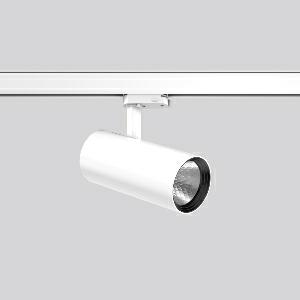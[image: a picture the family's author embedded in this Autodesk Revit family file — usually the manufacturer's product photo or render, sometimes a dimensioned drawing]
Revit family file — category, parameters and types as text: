
# Revit family: deecos_s_mini_742205_002_2_b299
name_source: partatom
category: Lighting Fixtures
units: mm (PartAtom-declared; Revit-internal decimal feet)

## family parameters
Cut with Voids When Loaded = No
Host = Face
Light Source = No
Part Type = Normal
Room Calculation Point = No
Round Connector Dimension = Use Diameter
Shared = No

## types (1)
- DEECOS S mini (1 x LED Modul 927, 3500 lm, 2700)
    Apparent Load = 29 VA
    Approval mark = CE
    CIE Flux Codes = 95 99 100 100 100
    Color Rendering = 92
    Color Temperature = 2700
    Default Elevation = 1800 mm
    Description = Series: DEECOS S mini
LED surface-mounted projector in modern design with no visible cooling ribs. Housing: die-cast aluminium, powder-coated. Rotation range: 356°. Swivel range: 90°. Black plastic ring and recessed LED to prevent glare from the side. Optical assembly with reflector made of MIRO-Silver with 98% total light reflection for outstanding efficiency - can be changed without tools. Best colour rendering index Ra>90. With multi adaptor for 3-circuit tracks 230 V. Suitable for Track on ceiling, Wall track. High quality converter without flickering and stroboscopic effect. The following accessories can be mounted without use of tools: interchangeable lenses, decorative glasses, honeycomb louvre, clear and frosted diffusers, white interchangeable plastic ring. 
Colour: traffic white, matt (RAL 9016)
Diameter: 87 mm
Height: 214 mm
Lamp: LED
Socket: without socket
Colour temperature: 2700K
Colour rendering index (CRI): 92
System power: 29 W
Rated luminous flux: 3500 lm
Luminous efficiency: 121 lm/W
Control gear: Regulated power supply
Protection class: I
Type of protection: IP 20
    Height = 214 mm
    Lamp = 1 x LED Modul 927
    Lamp Light Flux = 3500 lm
    Lamp count = 1
    Length = 87 mm
    Lifetime = 50000 h
    Luminous efficacy = 121 lm/W
    Manufacturer = RZB
    ModVariant = No
    Model = 742205.002.2
    Mounting Place = Ceiling
    Mounting Type = Rail mounted
    Number of Poles = 1
    OnlyDefault = Yes
    Power Factor = 1
    Product Name = DEECOS S mini
    Product group = Track mounted projectors
    ProductGroupID = 301
    Protection Class = Protection class I
    Protection Degree = IP 20
    RLX_Detail_Level = 1
    RLX_Emergency_Light_Flux = 0 lm
    RLX_Emergency_Type = 0
    RLX_Emergency_Type_DB = No
    RlxData = <blob elided: 35301 chars, md5=8d30d4c9>
    Socket = socket
    Standby Power = 0 W
    System Light Flux = 3500 lm
    System Power = 29 W
    Type Comments = Product without accessories
    Type Image = 741926.002.jpg
    URL = http://relux.com
    VarID = ---
    Voltage = 230 V
    Voltage Range = 220-240 V
    Weight = 0.00 kg
    Width = 0 mm  [stored 0 ft]

note: [stored X ft] marks values corroborated as IEEE doubles in the binary element streams (Revit-internal decimal feet)

## geometry (parser evidence)
native form markers: Blend x4, Sweep x12
no freeform markers — native parametric forms only
